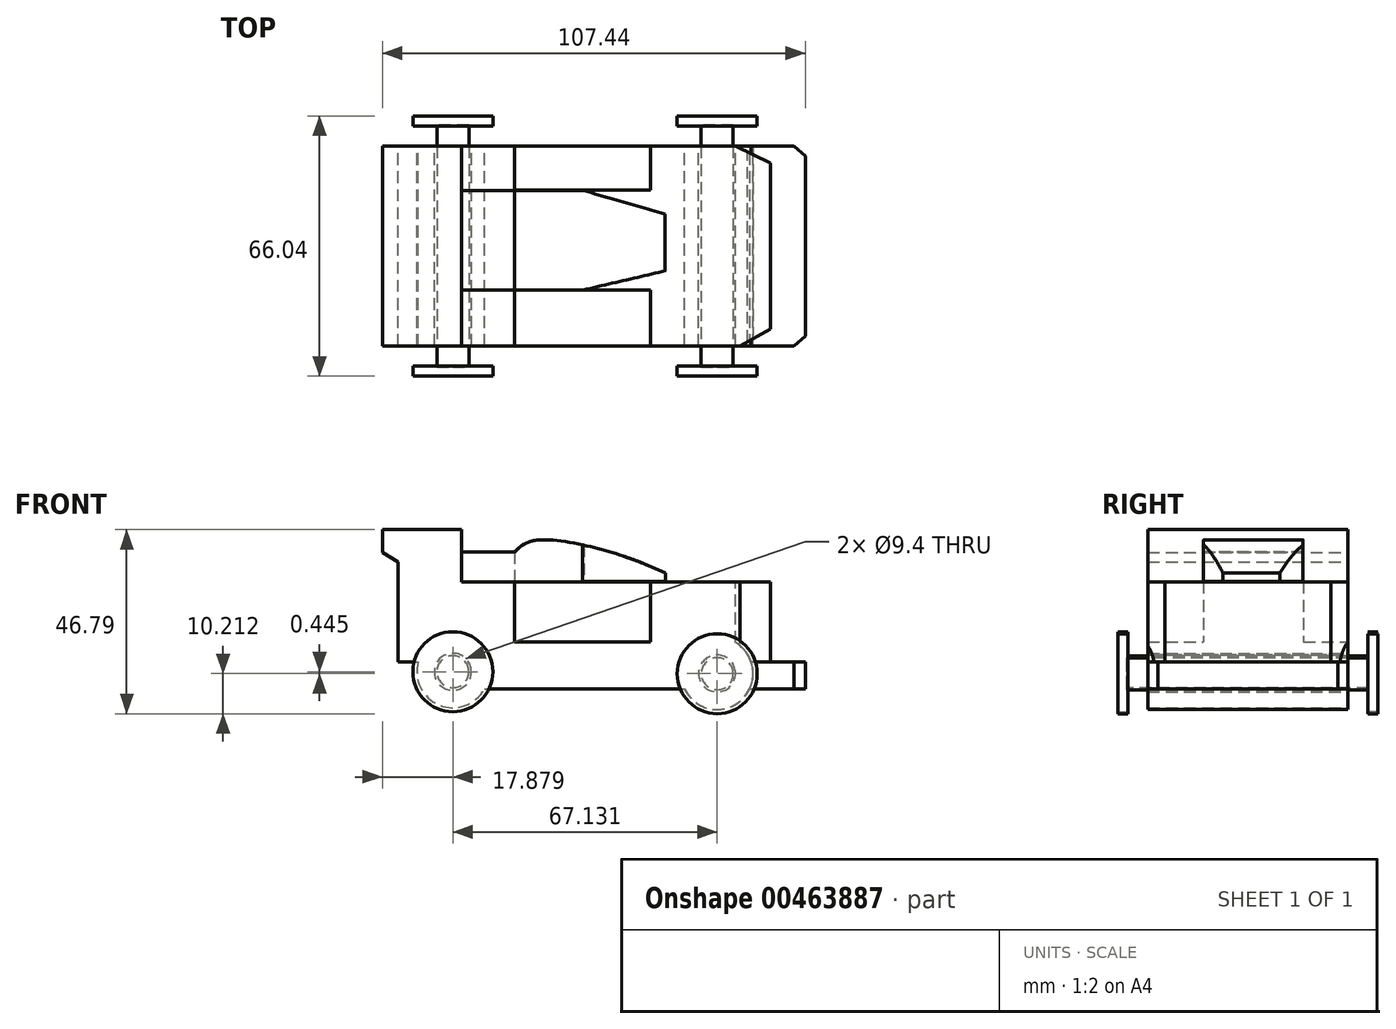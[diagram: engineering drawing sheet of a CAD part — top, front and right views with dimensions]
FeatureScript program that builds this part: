
annotation { "Feature Type Name" : "Feature", "Feature Type Description" : "" }
export const myFeature = defineFeature(function(context is Context, id is Id, definition is map)
    precondition{}
    {
        {
            var Q0;
            Q0=qCreatedBy(makeId("Front.planeOp"),FACE);
            var sketch = newSketch(context, id + "F0", { "sketchPlane" : qUnion([Q0])});
            skCircle(sketch, "E0", {"center": v(-30.53, -30.3) * mm, "radius": 9.14 * mm});
            skPoint(sketch, "E0.first.point", {"position": v(-22.47, -34.62) * mm});
            skPoint(sketch, "E0.second.point", {"position": v(-38.95, -26.72) * mm});
            skPoint(sketch, "E0.third.point", {"position": v(-21.57, -28.46) * mm});
            skCircle(sketch, "E1", {"center": v(36.63, -30.8) * mm, "radius": 9.14 * mm});
            skPoint(sketch, "E1.first.point", {"position": v(27.8, -28.46) * mm});
            skPoint(sketch, "E1.second.point", {"position": v(45.48, -28.46) * mm});
            skPoint(sketch, "E1.third.point", {"position": v(44.94, -34.62) * mm});
            skLineSegment(sketch, "E2", {"start": v(-22.47, -34.62) * mm, "end": v(28.33, -34.62) * mm});
            skLineSegment(sketch, "E3", {"start": v(44.94, -34.62) * mm, "end": v(59.03, -34.62) * mm});
            skLineSegment(sketch, "E4", {"start": v(59.03, -34.62) * mm, "end": v(59.03, -27.76) * mm});
            skLineSegment(sketch, "E5", {"start": v(59.03, -27.76) * mm, "end": v(50.14, -27.76) * mm});
            skLineSegment(sketch, "E6", {"start": v(50.14, -27.76) * mm, "end": v(50.14, -7.44) * mm});
            skLineSegment(sketch, "E7", {"start": v(50.14, -7.44) * mm, "end": v(19.66, -7.44) * mm});
            skLineSegment(sketch, "E8", {"start": v(19.66, -7.44) * mm, "end": v(19.66, -22.68) * mm});
            skLineSegment(sketch, "E9", {"start": v(19.66, -22.68) * mm, "end": v(-14.88, -22.68) * mm});
            skLineSegment(sketch, "E10", {"start": v(-14.88, -22.68) * mm, "end": v(-14.88, -7.44) * mm});
            skLineSegment(sketch, "E11", {"start": v(-14.88, -7.44) * mm, "end": v(-28.34, -7.44) * mm});
            skLineSegment(sketch, "E12", {"start": v(-28.34, -7.44) * mm, "end": v(-28.34, 5.84) * mm});
            skLineSegment(sketch, "E13", {"start": v(-28.34, 5.84) * mm, "end": v(-48.4, 5.84) * mm});
            skLineSegment(sketch, "E14", {"start": v(-48.4, 5.84) * mm, "end": v(-48.4, 0) * mm});
            skLineSegment(sketch, "E15", {"start": v(-48.4, 0) * mm, "end": v(-44.43, -2.36) * mm});
            skLineSegment(sketch, "E16", {"start": v(-44.43, -2.36) * mm, "end": v(-44.43, -27.76) * mm});
            skLineSegment(sketch, "E17", {"start": v(-44.43, -27.76) * mm, "end": v(-38.95, -27.76) * mm});
            skSolve(sketch);
        }
        {
            var Q0;
            Q0 = qSketchRegion(id + "F0", true);
            extrude(context, id + "F1", {"entities" : qUnion([Q0]), "depth" : 50.8 * mm});
        }
        {
            var Q0;
            Q0=makeQuery(id+"F1.opExtrude","CAP_FACE",FACE,{"disambiguationData":[OSD([sQuery(id+"F0.wireOp",EDGE,"E0"),sQuery(id+"F0.wireOp",EDGE,"E1"),sQuery(id+"F0.wireOp",EDGE,"E2"),sQuery(id+"F0.wireOp",EDGE,"E3"),sQuery(id+"F0.wireOp",EDGE,"E4"),sQuery(id+"F0.wireOp",EDGE,"E5"),sQuery(id+"F0.wireOp",EDGE,"E6"),sQuery(id+"F0.wireOp",EDGE,"E7"),sQuery(id+"F0.wireOp",EDGE,"E8"),sQuery(id+"F0.wireOp",EDGE,"E9"),sQuery(id+"F0.wireOp",EDGE,"E10"),sQuery(id+"F0.wireOp",EDGE,"E11"),sQuery(id+"F0.wireOp",EDGE,"E12"),sQuery(id+"F0.wireOp",EDGE,"E13"),sQuery(id+"F0.wireOp",EDGE,"E14"),sQuery(id+"F0.wireOp",EDGE,"E15"),sQuery(id+"F0.wireOp",EDGE,"E16"),sQuery(id+"F0.wireOp",EDGE,"E17")])],"isStart":false});
            var sketch = newSketch(context, id + "F2", { "sketchPlane" : qUnion([Q0])});
            skCircle(sketch, "E18", {"center": v(-30.53, -30.3) * mm, "radius": 9.14 * mm});
            skCircle(sketch, "E19", {"center": v(36.63, -30.8) * mm, "radius": 9.14 * mm});
            skSolve(sketch);
        }
        {
            var Q0;
            Q0 = qSketchRegion(id + "F2", true);
            extrude(context, id + "F3", {"entities" : qUnion([Q0]), "operationType" : NewBodyOperationType.REMOVE, "oppositeDirection" : true, "depth" : 54.86 * mm});
        }
        {
            var Q0;
            Q0=makeQuery(id+"F1.opExtrude","CAP_FACE",FACE,{"disambiguationData":[OSD([sQuery(id+"F0.wireOp",EDGE,"E0"),sQuery(id+"F0.wireOp",EDGE,"E1"),sQuery(id+"F0.wireOp",EDGE,"E2"),sQuery(id+"F0.wireOp",EDGE,"E3"),sQuery(id+"F0.wireOp",EDGE,"E4"),sQuery(id+"F0.wireOp",EDGE,"E5"),sQuery(id+"F0.wireOp",EDGE,"E6"),sQuery(id+"F0.wireOp",EDGE,"E7"),sQuery(id+"F0.wireOp",EDGE,"E8"),sQuery(id+"F0.wireOp",EDGE,"E9"),sQuery(id+"F0.wireOp",EDGE,"E10"),sQuery(id+"F0.wireOp",EDGE,"E11"),sQuery(id+"F0.wireOp",EDGE,"E12"),sQuery(id+"F0.wireOp",EDGE,"E13"),sQuery(id+"F0.wireOp",EDGE,"E14"),sQuery(id+"F0.wireOp",EDGE,"E15"),sQuery(id+"F0.wireOp",EDGE,"E16"),sQuery(id+"F0.wireOp",EDGE,"E17")])],"isStart":false});
            var sketch = newSketch(context, id + "F4", { "sketchPlane" : qUnion([Q0])});
            skCircle(sketch, "E20", {"center": v(36.63, -30.8) * mm, "radius": 4.06 * mm});
            skCircle(sketch, "E21", {"center": v(-30.53, -30.3) * mm, "radius": 4.06 * mm});
            skSolve(sketch);
        }
        {
            var Q0;
            Q0 = qSketchRegion(id + "F4", true);
            extrude(context, id + "F5", {"entities" : qUnion([Q0]), "oppositeDirection" : true, "depth" : 56.13 * mm, "hasSecondDirection" : true, "secondDirectionOppositeDirection" : false, "secondDirectionDepth" : 5.33 * mm});
        }
        {
            var Q0;
            Q0=makeQuery(id+"F1.opExtrude","CAP_FACE",FACE,{"disambiguationData":[OSD([sQuery(id+"F0.wireOp",EDGE,"E0"),sQuery(id+"F0.wireOp",EDGE,"E1"),sQuery(id+"F0.wireOp",EDGE,"E2"),sQuery(id+"F0.wireOp",EDGE,"E3"),sQuery(id+"F0.wireOp",EDGE,"E4"),sQuery(id+"F0.wireOp",EDGE,"E5"),sQuery(id+"F0.wireOp",EDGE,"E6"),sQuery(id+"F0.wireOp",EDGE,"E7"),sQuery(id+"F0.wireOp",EDGE,"E8"),sQuery(id+"F0.wireOp",EDGE,"E9"),sQuery(id+"F0.wireOp",EDGE,"E10"),sQuery(id+"F0.wireOp",EDGE,"E11"),sQuery(id+"F0.wireOp",EDGE,"E12"),sQuery(id+"F0.wireOp",EDGE,"E13"),sQuery(id+"F0.wireOp",EDGE,"E14"),sQuery(id+"F0.wireOp",EDGE,"E15"),sQuery(id+"F0.wireOp",EDGE,"E16"),sQuery(id+"F0.wireOp",EDGE,"E17")])],"isStart":false});
            var sketch = newSketch(context, id + "F6", { "sketchPlane" : qUnion([Q0])});
            skCircle(sketch, "E22", {"center": v(-30.53, -30.3) * mm, "radius": 10.16 * mm});
            skCircle(sketch, "E23", {"center": v(36.63, -30.8) * mm, "radius": 10.16 * mm});
            skSolve(sketch);
        }
        {
            var Q0;
            Q0 = qSketchRegion(id + "F6", true);
            extrude(context, id + "F7", {"entities" : qUnion([Q0]), "depth" : 7.62 * mm, "hasSecondDirection" : true, "secondDirectionOppositeDirection" : false, "secondDirectionDepth" : 5.08 * mm});
        }
        {
            var Q0;
            Q0=makeQuery(id+"F1.opExtrude","CAP_FACE",FACE,{"disambiguationData":[OSD([sQuery(id+"F0.wireOp",EDGE,"E0"),sQuery(id+"F0.wireOp",EDGE,"E1"),sQuery(id+"F0.wireOp",EDGE,"E2"),sQuery(id+"F0.wireOp",EDGE,"E3"),sQuery(id+"F0.wireOp",EDGE,"E4"),sQuery(id+"F0.wireOp",EDGE,"E5"),sQuery(id+"F0.wireOp",EDGE,"E6"),sQuery(id+"F0.wireOp",EDGE,"E7"),sQuery(id+"F0.wireOp",EDGE,"E8"),sQuery(id+"F0.wireOp",EDGE,"E9"),sQuery(id+"F0.wireOp",EDGE,"E10"),sQuery(id+"F0.wireOp",EDGE,"E11"),sQuery(id+"F0.wireOp",EDGE,"E12"),sQuery(id+"F0.wireOp",EDGE,"E13"),sQuery(id+"F0.wireOp",EDGE,"E14"),sQuery(id+"F0.wireOp",EDGE,"E15"),sQuery(id+"F0.wireOp",EDGE,"E16"),sQuery(id+"F0.wireOp",EDGE,"E17")])],"isStart":true});
            var sketch = newSketch(context, id + "F8", { "sketchPlane" : qUnion([Q0])});
            skCircle(sketch, "E24", {"center": v(-36.63, -30.8) * mm, "radius": 10.16 * mm});
            skCircle(sketch, "E25", {"center": v(30.53, -30.3) * mm, "radius": 10.16 * mm});
            skSolve(sketch);
        }
        {
            var Q0;
            Q0 = qSketchRegion(id + "F8", true);
            extrude(context, id + "F9", {"entities" : qUnion([Q0]), "depth" : 7.62 * mm, "hasSecondDirection" : true, "secondDirectionOppositeDirection" : false, "secondDirectionDepth" : 5.08 * mm});
        }
        {
            var Q0;
            Q0=makeQuery(id+"F1.opExtrude","SWEPT_FACE",FACE,{"disambiguationData":[OSD([sQuery(id+"F0.wireOp",EDGE,"E9")])]});
            var sketch = newSketch(context, id + "F10", { "sketchPlane" : qUnion([Q0])});
            skLineSegment(sketch, "E26.bottom", {"start": v(-14.88, -11.2) * mm, "end": v(19.66, -11.2) * mm});
            skLineSegment(sketch, "E26.top", {"start": v(-14.88, -36.6) * mm, "end": v(19.66, -36.6) * mm});
            skLineSegment(sketch, "E26.left", {"start": v(-14.88, -11.2) * mm, "end": v(-14.88, -36.6) * mm});
            skLineSegment(sketch, "E26.right", {"start": v(19.66, -11.2) * mm, "end": v(19.66, -36.6) * mm});
            skSolve(sketch);
        }
        {
            var Q0;
            Q0 = qSketchRegion(id + "F10", true);
            extrude(context, id + "F11", {"entities" : qUnion([Q0]), "operationType" : NewBodyOperationType.ADD, "depth" : 15.24 * mm});
        }
        {
            var Q0;
            Q0=makeQuery(id+"F11.boolean.opBoolean","MERGE",FACE,{"derivedFrom":[makeQuery(id+"F1.opExtrude","SWEPT_FACE",FACE,{"disambiguationData":[OSD([sQuery(id+"F0.wireOp",EDGE,"E7")])]}),makeQuery(id+"F1.opExtrude","SWEPT_FACE",FACE,{"disambiguationData":[OSD([sQuery(id+"F0.wireOp",EDGE,"E11")])]}),makeQuery(id+"F11.opExtrude","CAP_FACE",FACE,{"disambiguationData":[OSD([sQuery(id+"F10.wireOp",EDGE,"E26.bottom"),sQuery(id+"F10.wireOp",EDGE,"E26.top"),sQuery(id+"F10.wireOp",EDGE,"E26.left"),sQuery(id+"F10.wireOp",EDGE,"E26.right")])],"isStart":false})]});
            var sketch = newSketch(context, id + "F12", { "sketchPlane" : qUnion([Q0])});
            skLineSegment(sketch, "E27.bottom", {"start": v(-28.34, -11.32) * mm, "end": v(-14.88, -11.32) * mm});
            skLineSegment(sketch, "E27.top", {"start": v(-28.34, -36.6) * mm, "end": v(-14.88, -36.6) * mm});
            skLineSegment(sketch, "E27.left", {"start": v(-28.34, -11.32) * mm, "end": v(-28.34, -36.6) * mm});
            skLineSegment(sketch, "E27.right", {"start": v(-14.88, -11.32) * mm, "end": v(-14.88, -36.6) * mm});
            skSolve(sketch);
        }
        {
            var Q0;
            Q0 = qSketchRegion(id + "F12", true);
            extrude(context, id + "F13", {"entities" : qUnion([Q0]), "operationType" : NewBodyOperationType.ADD, "depth" : 7.62 * mm});
        }
        {
            var Q0;
            Q0=makeQuery(id+"F11.opExtrude","SWEPT_FACE",FACE,{"disambiguationData":[OSD([sQuery(id+"F10.wireOp",EDGE,"E26.top")])]});
            var sketch = newSketch(context, id + "F14", { "sketchPlane" : qUnion([Q0])});
            skFitSpline(sketch, "E28", {"points": [v(-14.95, 0) * mm, v(-9.97, 3.02) * mm, v(9.97, 0) * mm, v(21.32, -4.26) * mm, v(28.47, -7.34) * mm], "startDerivative": vector(20.38, 20.97) * mm, "endDerivative": vector(33.05, -14.25) * mm});
            skLineSegment(sketch, "E29", {"start": v(28.47, -7.34) * mm, "end": v(-14.88, -7.44) * mm});
            skLineSegment(sketch, "E30", {"start": v(-14.88, -7.44) * mm, "end": v(-14.95, 0) * mm});
            skSolve(sketch);
        }
        {
            var Q0;
            Q0 = qSketchRegion(id + "F14", true);
            extrude(context, id + "F15", {"entities" : qUnion([Q0]), "operationType" : NewBodyOperationType.ADD, "oppositeDirection" : true, "depth" : 25.27 * mm});
        }
        {
            var Q0;
            {var subQ0=sQuery(id+"F10.wireOp",EDGE,"E26.top");var subQ1=sQuery(id+"F10.wireOp",EDGE,"E26.bottom");var subQ2=makeQuery(id+"F11.opExtrude","CAP_FACE",FACE,{"disambiguationData":[OSD([subQ1,subQ0,sQuery(id+"F10.wireOp",EDGE,"E26.left"),sQuery(id+"F10.wireOp",EDGE,"E26.right")])],"isStart":false});var subQ3=sQuery(id+"F0.wireOp",EDGE,"E6");var subQ4=sQuery(id+"F0.wireOp",EDGE,"E12");var subQ5=sQuery(id+"F0.wireOp",EDGE,"E8");var subQ6=sQuery(id+"F0.wireOp",EDGE,"E10");var subQ7=sQuery(id+"F0.wireOp",EDGE,"E17");var subQ8=sQuery(id+"F0.wireOp",EDGE,"E16");var subQ9=sQuery(id+"F0.wireOp",EDGE,"E15");var subQ10=sQuery(id+"F0.wireOp",EDGE,"E14");var subQ11=sQuery(id+"F0.wireOp",EDGE,"E13");var subQ12=sQuery(id+"F0.wireOp",EDGE,"E11");var subQ13=sQuery(id+"F0.wireOp",EDGE,"E9");var subQ14=sQuery(id+"F0.wireOp",EDGE,"E7");var subQ15=sQuery(id+"F0.wireOp",EDGE,"E5");var subQ16=sQuery(id+"F0.wireOp",EDGE,"E4");var subQ17=sQuery(id+"F0.wireOp",EDGE,"E3");var subQ18=sQuery(id+"F0.wireOp",EDGE,"E2");var subQ19=sQuery(id+"F0.wireOp",EDGE,"E1");var subQ20=sQuery(id+"F0.wireOp",EDGE,"E0");var subQ21=makeQuery(id+"F1.opExtrude","SWEPT_FACE",FACE,{"disambiguationData":[OSD([subQ12])]});var subQ22=makeQuery(id+"F1.opExtrude","SWEPT_FACE",FACE,{"disambiguationData":[OSD([subQ14])]});Q0=makeQuery(id+"F13.boolean.opBoolean","SPLIT",FACE,{"disambiguationData":[TD([makeQuery(id+"F1.opExtrude","CAP_FACE",FACE,{"disambiguationData":[OSD([subQ20,subQ19,subQ18,subQ17,subQ16,subQ15,subQ3,subQ14,subQ5,subQ13,subQ6,subQ12,subQ4,subQ11,subQ10,subQ9,subQ8,subQ7])],"isStart":true}),makeQuery(id+"F1.opExtrude","CAP_FACE",FACE,{"disambiguationData":[OSD([subQ20,subQ19,subQ18,subQ17,subQ16,subQ15,subQ3,subQ14,subQ5,subQ13,subQ6,subQ12,subQ4,subQ11,subQ10,subQ9,subQ8,subQ7])],"isStart":false}),makeQuery(id+"F1.opExtrude","SWEPT_FACE",FACE,{"disambiguationData":[OSD([subQ3])]}),subQ22,makeQuery(id+"F1.opExtrude","SWEPT_FACE",FACE,{"disambiguationData":[OSD([subQ5])]}),makeQuery(id+"F1.opExtrude","SWEPT_FACE",FACE,{"disambiguationData":[OSD([subQ6])]}),subQ21,makeQuery(id+"F1.opExtrude","SWEPT_FACE",FACE,{"disambiguationData":[OSD([subQ4])]}),makeQuery(id+"F11.opExtrude","SWEPT_FACE",FACE,{"disambiguationData":[OSD([subQ1])]}),subQ2,makeQuery(id+"F11.opExtrude","SWEPT_FACE",FACE,{"disambiguationData":[OSD([subQ0])]}),makeQuery(id+"F13.opExtrude","SWEPT_FACE",FACE,{"disambiguationData":[OSD([sQuery(id+"F12.wireOp",EDGE,"E27.bottom")])]}),makeQuery(id+"F13.opExtrude","SWEPT_FACE",FACE,{"disambiguationData":[OSD([sQuery(id+"F12.wireOp",EDGE,"E27.top")])]}),makeQuery(id+"F13.opExtrude","SWEPT_FACE",FACE,{"disambiguationData":[OSD([sQuery(id+"F12.wireOp",EDGE,"E27.right")])]})])],"derivedFrom":makeQuery(id+"F11.boolean.opBoolean","MERGE",FACE,{"derivedFrom":[subQ22,subQ21,subQ2]})});}
            var sketch = newSketch(context, id + "F16", { "sketchPlane" : qUnion([Q0])});
            skLineSegment(sketch, "E31", {"start": v(28.7, -18.8) * mm, "end": v(28.73, -11.19) * mm});
            skLineSegment(sketch, "E32", {"start": v(28.73, -30.45) * mm, "end": v(28.7, -38.07) * mm});
            skLineSegment(sketch, "E33", {"start": v(28.73, -30.45) * mm, "end": v(2.4, -36.6) * mm});
            skLineSegment(sketch, "E34", {"start": v(2.4, -36.6) * mm, "end": v(28.7, -38.07) * mm});
            skLineSegment(sketch, "E35", {"start": v(28.7, -18.8) * mm, "end": v(2.4, -11.2) * mm});
            skLineSegment(sketch, "E36", {"start": v(2.4, -11.2) * mm, "end": v(28.73, -11.19) * mm});
            skSolve(sketch);
        }
        {
            var Q0;
            Q0 = qSketchRegion(id + "F16", true);
            extrude(context, id + "F17", {"entities" : qUnion([Q0]), "operationType" : NewBodyOperationType.REMOVE, "depth" : 9.37 * mm});
        }
        {
            var Q0;
            {var subQ0=sQuery(id+"F10.wireOp",EDGE,"E26.top");var subQ1=sQuery(id+"F10.wireOp",EDGE,"E26.bottom");var subQ2=makeQuery(id+"F11.opExtrude","CAP_FACE",FACE,{"disambiguationData":[OSD([subQ1,subQ0,sQuery(id+"F10.wireOp",EDGE,"E26.left"),sQuery(id+"F10.wireOp",EDGE,"E26.right")])],"isStart":false});var subQ3=sQuery(id+"F0.wireOp",EDGE,"E6");var subQ4=sQuery(id+"F0.wireOp",EDGE,"E12");var subQ5=sQuery(id+"F0.wireOp",EDGE,"E8");var subQ6=sQuery(id+"F0.wireOp",EDGE,"E10");var subQ7=sQuery(id+"F0.wireOp",EDGE,"E17");var subQ8=sQuery(id+"F0.wireOp",EDGE,"E16");var subQ9=sQuery(id+"F0.wireOp",EDGE,"E15");var subQ10=sQuery(id+"F0.wireOp",EDGE,"E14");var subQ11=sQuery(id+"F0.wireOp",EDGE,"E13");var subQ12=sQuery(id+"F0.wireOp",EDGE,"E11");var subQ13=sQuery(id+"F0.wireOp",EDGE,"E9");var subQ14=sQuery(id+"F0.wireOp",EDGE,"E7");var subQ15=sQuery(id+"F0.wireOp",EDGE,"E5");var subQ16=sQuery(id+"F0.wireOp",EDGE,"E4");var subQ17=sQuery(id+"F0.wireOp",EDGE,"E3");var subQ18=sQuery(id+"F0.wireOp",EDGE,"E2");var subQ19=sQuery(id+"F0.wireOp",EDGE,"E1");var subQ20=sQuery(id+"F0.wireOp",EDGE,"E0");var subQ21=makeQuery(id+"F1.opExtrude","SWEPT_FACE",FACE,{"disambiguationData":[OSD([subQ12])]});var subQ22=makeQuery(id+"F1.opExtrude","SWEPT_FACE",FACE,{"disambiguationData":[OSD([subQ14])]});Q0=makeQuery(id+"F13.boolean.opBoolean","SPLIT",FACE,{"disambiguationData":[TD([makeQuery(id+"F1.opExtrude","CAP_FACE",FACE,{"disambiguationData":[OSD([subQ20,subQ19,subQ18,subQ17,subQ16,subQ15,subQ3,subQ14,subQ5,subQ13,subQ6,subQ12,subQ4,subQ11,subQ10,subQ9,subQ8,subQ7])],"isStart":true}),makeQuery(id+"F1.opExtrude","CAP_FACE",FACE,{"disambiguationData":[OSD([subQ20,subQ19,subQ18,subQ17,subQ16,subQ15,subQ3,subQ14,subQ5,subQ13,subQ6,subQ12,subQ4,subQ11,subQ10,subQ9,subQ8,subQ7])],"isStart":false}),makeQuery(id+"F1.opExtrude","SWEPT_FACE",FACE,{"disambiguationData":[OSD([subQ3])]}),subQ22,makeQuery(id+"F1.opExtrude","SWEPT_FACE",FACE,{"disambiguationData":[OSD([subQ5])]}),makeQuery(id+"F1.opExtrude","SWEPT_FACE",FACE,{"disambiguationData":[OSD([subQ6])]}),subQ21,makeQuery(id+"F1.opExtrude","SWEPT_FACE",FACE,{"disambiguationData":[OSD([subQ4])]}),makeQuery(id+"F11.opExtrude","SWEPT_FACE",FACE,{"disambiguationData":[OSD([subQ1])]}),subQ2,makeQuery(id+"F11.opExtrude","SWEPT_FACE",FACE,{"disambiguationData":[OSD([subQ0])]}),makeQuery(id+"F13.opExtrude","SWEPT_FACE",FACE,{"disambiguationData":[OSD([sQuery(id+"F12.wireOp",EDGE,"E27.bottom")])]}),makeQuery(id+"F13.opExtrude","SWEPT_FACE",FACE,{"disambiguationData":[OSD([sQuery(id+"F12.wireOp",EDGE,"E27.top")])]}),makeQuery(id+"F13.opExtrude","SWEPT_FACE",FACE,{"disambiguationData":[OSD([sQuery(id+"F12.wireOp",EDGE,"E27.right")])]})])],"derivedFrom":makeQuery(id+"F11.boolean.opBoolean","MERGE",FACE,{"derivedFrom":[subQ22,subQ21,subQ2]})});}
            var sketch = newSketch(context, id + "F18", { "sketchPlane" : qUnion([Q0])});
            skLineSegment(sketch, "E37", {"start": v(50.14, 0) * mm, "end": v(41.25, 0) * mm});
            skLineSegment(sketch, "E38", {"start": v(41.25, 0) * mm, "end": v(50.14, -4.32) * mm});
            skLineSegment(sketch, "E39", {"start": v(50.14, -4.32) * mm, "end": v(50.14, 0) * mm});
            skLineSegment(sketch, "E40", {"start": v(50.14, -50.8) * mm, "end": v(42.37, -50.8) * mm});
            skLineSegment(sketch, "E41", {"start": v(42.37, -50.8) * mm, "end": v(50.14, -46.48) * mm});
            skLineSegment(sketch, "E42", {"start": v(50.14, -46.48) * mm, "end": v(50.14, -50.8) * mm});
            skSolve(sketch);
        }
        {
            var Q0;
            Q0 = qSketchRegion(id + "F18", true);
            extrude(context, id + "F19", {"entities" : qUnion([Q0]), "operationType" : NewBodyOperationType.REMOVE, "oppositeDirection" : true, "depth" : 20.32 * mm});
        }
        {
            var Q0;
            {var subQ0=sQuery(id+"F0.wireOp",EDGE,"E15");var subQ1=sQuery(id+"F0.wireOp",EDGE,"E14");var subQ2=sQuery(id+"F0.wireOp",EDGE,"E12");var subQ3=sQuery(id+"F0.wireOp",EDGE,"E11");var subQ4=sQuery(id+"F0.wireOp",EDGE,"E10");var subQ5=sQuery(id+"F0.wireOp",EDGE,"E13");var subQ6=sQuery(id+"F0.wireOp",EDGE,"E2");var subQ7=sQuery(id+"F0.wireOp",EDGE,"E7");var subQ8=sQuery(id+"F0.wireOp",EDGE,"E8");var subQ9=sQuery(id+"F0.wireOp",EDGE,"E9");var subQ10=sQuery(id+"F0.wireOp",EDGE,"E16");var subQ11=sQuery(id+"F0.wireOp",EDGE,"E17");Q0=makeQuery(id+"F19.boolean.opBoolean","SPLIT",FACE,{"disambiguationData":[TD([makeQuery(id+"F1.opExtrude","SWEPT_FACE",FACE,{"disambiguationData":[OSD([subQ6])]})])],"derivedFrom":makeQuery(id+"F1.opExtrude","CAP_FACE",FACE,{"disambiguationData":[OSD([sQuery(id+"F0.wireOp",EDGE,"E0"),sQuery(id+"F0.wireOp",EDGE,"E1"),subQ6,sQuery(id+"F0.wireOp",EDGE,"E3"),sQuery(id+"F0.wireOp",EDGE,"E4"),sQuery(id+"F0.wireOp",EDGE,"E5"),sQuery(id+"F0.wireOp",EDGE,"E6"),subQ7,subQ8,subQ9,subQ4,subQ3,subQ2,subQ5,subQ1,subQ0,subQ10,subQ11])],"isStart":true})});}
            var sketch = newSketch(context, id + "F20", { "sketchPlane" : qUnion([Q0])});
            skCircle(sketch, "E43", {"center": v(30.53, -30.3) * mm, "radius": 9.14 * mm});
            skPoint(sketch, "E43.first.point", {"position": v(39.32, -27.76) * mm});
            skPoint(sketch, "E43.second.point", {"position": v(33.47, -21.64) * mm});
            skPoint(sketch, "E43.third.point", {"position": v(22.47, -34.62) * mm});
            skCircle(sketch, "E44.0", {"center": v(30.53, -30.3) * mm, "radius": 4.7 * mm});
            skCircle(sketch, "E45", {"center": v(-36.6, -30.74) * mm, "radius": 9.14 * mm});
            skCircle(sketch, "E46.0", {"center": v(-36.6, -30.74) * mm, "radius": 4.7 * mm});
            skSolve(sketch);
        }
        {
            var Q0;
            Q0 = qSketchRegion(id + "F20", true);
            extrude(context, id + "F21", {"entities" : qUnion([Q0]), "operationType" : NewBodyOperationType.ADD, "oppositeDirection" : true, "depth" : 50.8 * mm});
        }
        {
            var Q0;
            {var subQ0=sQuery(id+"F10.wireOp",EDGE,"E26.top");var subQ1=sQuery(id+"F10.wireOp",EDGE,"E26.bottom");var subQ2=makeQuery(id+"F11.opExtrude","CAP_FACE",FACE,{"disambiguationData":[OSD([subQ1,subQ0,sQuery(id+"F10.wireOp",EDGE,"E26.left"),sQuery(id+"F10.wireOp",EDGE,"E26.right")])],"isStart":false});var subQ3=sQuery(id+"F0.wireOp",EDGE,"E6");var subQ4=sQuery(id+"F0.wireOp",EDGE,"E12");var subQ5=sQuery(id+"F0.wireOp",EDGE,"E8");var subQ6=sQuery(id+"F0.wireOp",EDGE,"E10");var subQ7=sQuery(id+"F0.wireOp",EDGE,"E17");var subQ8=sQuery(id+"F0.wireOp",EDGE,"E16");var subQ9=sQuery(id+"F0.wireOp",EDGE,"E15");var subQ10=sQuery(id+"F0.wireOp",EDGE,"E14");var subQ11=sQuery(id+"F0.wireOp",EDGE,"E13");var subQ12=sQuery(id+"F0.wireOp",EDGE,"E11");var subQ13=sQuery(id+"F0.wireOp",EDGE,"E9");var subQ14=sQuery(id+"F0.wireOp",EDGE,"E7");var subQ15=sQuery(id+"F0.wireOp",EDGE,"E5");var subQ16=sQuery(id+"F0.wireOp",EDGE,"E4");var subQ17=sQuery(id+"F0.wireOp",EDGE,"E3");var subQ18=sQuery(id+"F0.wireOp",EDGE,"E2");var subQ19=sQuery(id+"F0.wireOp",EDGE,"E1");var subQ20=sQuery(id+"F0.wireOp",EDGE,"E0");var subQ21=makeQuery(id+"F1.opExtrude","SWEPT_FACE",FACE,{"disambiguationData":[OSD([subQ12])]});var subQ22=makeQuery(id+"F1.opExtrude","SWEPT_FACE",FACE,{"disambiguationData":[OSD([subQ14])]});Q0=makeQuery(id+"F13.boolean.opBoolean","SPLIT",FACE,{"disambiguationData":[TD([makeQuery(id+"F1.opExtrude","CAP_FACE",FACE,{"disambiguationData":[OSD([subQ20,subQ19,subQ18,subQ17,subQ16,subQ15,subQ3,subQ14,subQ5,subQ13,subQ6,subQ12,subQ4,subQ11,subQ10,subQ9,subQ8,subQ7])],"isStart":true}),makeQuery(id+"F1.opExtrude","CAP_FACE",FACE,{"disambiguationData":[OSD([subQ20,subQ19,subQ18,subQ17,subQ16,subQ15,subQ3,subQ14,subQ5,subQ13,subQ6,subQ12,subQ4,subQ11,subQ10,subQ9,subQ8,subQ7])],"isStart":false}),makeQuery(id+"F1.opExtrude","SWEPT_FACE",FACE,{"disambiguationData":[OSD([subQ3])]}),subQ22,makeQuery(id+"F1.opExtrude","SWEPT_FACE",FACE,{"disambiguationData":[OSD([subQ5])]}),makeQuery(id+"F1.opExtrude","SWEPT_FACE",FACE,{"disambiguationData":[OSD([subQ6])]}),subQ21,makeQuery(id+"F1.opExtrude","SWEPT_FACE",FACE,{"disambiguationData":[OSD([subQ4])]}),makeQuery(id+"F11.opExtrude","SWEPT_FACE",FACE,{"disambiguationData":[OSD([subQ1])]}),subQ2,makeQuery(id+"F11.opExtrude","SWEPT_FACE",FACE,{"disambiguationData":[OSD([subQ0])]}),makeQuery(id+"F13.opExtrude","SWEPT_FACE",FACE,{"disambiguationData":[OSD([sQuery(id+"F12.wireOp",EDGE,"E27.bottom")])]}),makeQuery(id+"F13.opExtrude","SWEPT_FACE",FACE,{"disambiguationData":[OSD([sQuery(id+"F12.wireOp",EDGE,"E27.top")])]}),makeQuery(id+"F13.opExtrude","SWEPT_FACE",FACE,{"disambiguationData":[OSD([sQuery(id+"F12.wireOp",EDGE,"E27.right")])]})])],"derivedFrom":makeQuery(id+"F11.boolean.opBoolean","MERGE",FACE,{"derivedFrom":[subQ22,subQ21,subQ2]})});}
            var sketch = newSketch(context, id + "F22", { "sketchPlane" : qUnion([Q0])});
            skLineSegment(sketch, "E47.bottom", {"start": v(23.35, -17.23) * mm, "end": v(30.33, -17.23) * mm});
            skLineSegment(sketch, "E47.top", {"start": v(23.35, -31.67) * mm, "end": v(30.33, -31.67) * mm});
            skLineSegment(sketch, "E47.left", {"start": v(23.35, -17.23) * mm, "end": v(23.35, -31.67) * mm});
            skLineSegment(sketch, "E47.right", {"start": v(30.33, -17.23) * mm, "end": v(30.33, -31.67) * mm});
            skSolve(sketch);
        }
        {
            var Q0;
            Q0 = qSketchRegion(id + "F22", true);
            extrude(context, id + "F23", {"entities" : qUnion([Q0]), "operationType" : NewBodyOperationType.REMOVE, "depth" : 11.18 * mm});
        }
        {
            var Q0;
            Q0=makeQuery(id+"F19.boolean.opBoolean","MERGE",FACE,{"derivedFrom":[makeQuery(id+"F1.opExtrude","SWEPT_FACE",FACE,{"disambiguationData":[OSD([sQuery(id+"F0.wireOp",EDGE,"E5")])]}),makeQuery(id+"F19.opExtrude","CAP_FACE",FACE,{"disambiguationData":[OSD([sQuery(id+"F18.wireOp",EDGE,"E37"),sQuery(id+"F18.wireOp",EDGE,"E38"),sQuery(id+"F18.wireOp",EDGE,"E39")])],"isStart":false}),makeQuery(id+"F19.opExtrude","CAP_FACE",FACE,{"disambiguationData":[OSD([sQuery(id+"F18.wireOp",EDGE,"E40"),sQuery(id+"F18.wireOp",EDGE,"E41"),sQuery(id+"F18.wireOp",EDGE,"E42")])],"isStart":false})]});
            var sketch = newSketch(context, id + "F24", { "sketchPlane" : qUnion([Q0])});
            skLineSegment(sketch, "E48", {"start": v(56.14, 0) * mm, "end": v(59.03, -2.55) * mm});
            skLineSegment(sketch, "E49", {"start": v(59.03, 0) * mm, "end": v(56.14, 0) * mm});
            skLineSegment(sketch, "E50", {"start": v(56.15, -50.8) * mm, "end": v(59.03, -48.23) * mm});
            skLineSegment(sketch, "E51", {"start": v(59.03, -48.23) * mm, "end": v(59.03, -50.8) * mm});
            skLineSegment(sketch, "E52", {"start": v(59.03, -2.55) * mm, "end": v(59.03, 0) * mm});
            skLineSegment(sketch, "E53", {"start": v(56.15, -50.8) * mm, "end": v(59.03, -50.8) * mm});
            skSolve(sketch);
        }
        {
            var Q0;
            Q0 = qSketchRegion(id + "F24", true);
            extrude(context, id + "F25", {"entities" : qUnion([Q0]), "operationType" : NewBodyOperationType.REMOVE, "oppositeDirection" : true, "depth" : 25.4 * mm});
        }
    });
